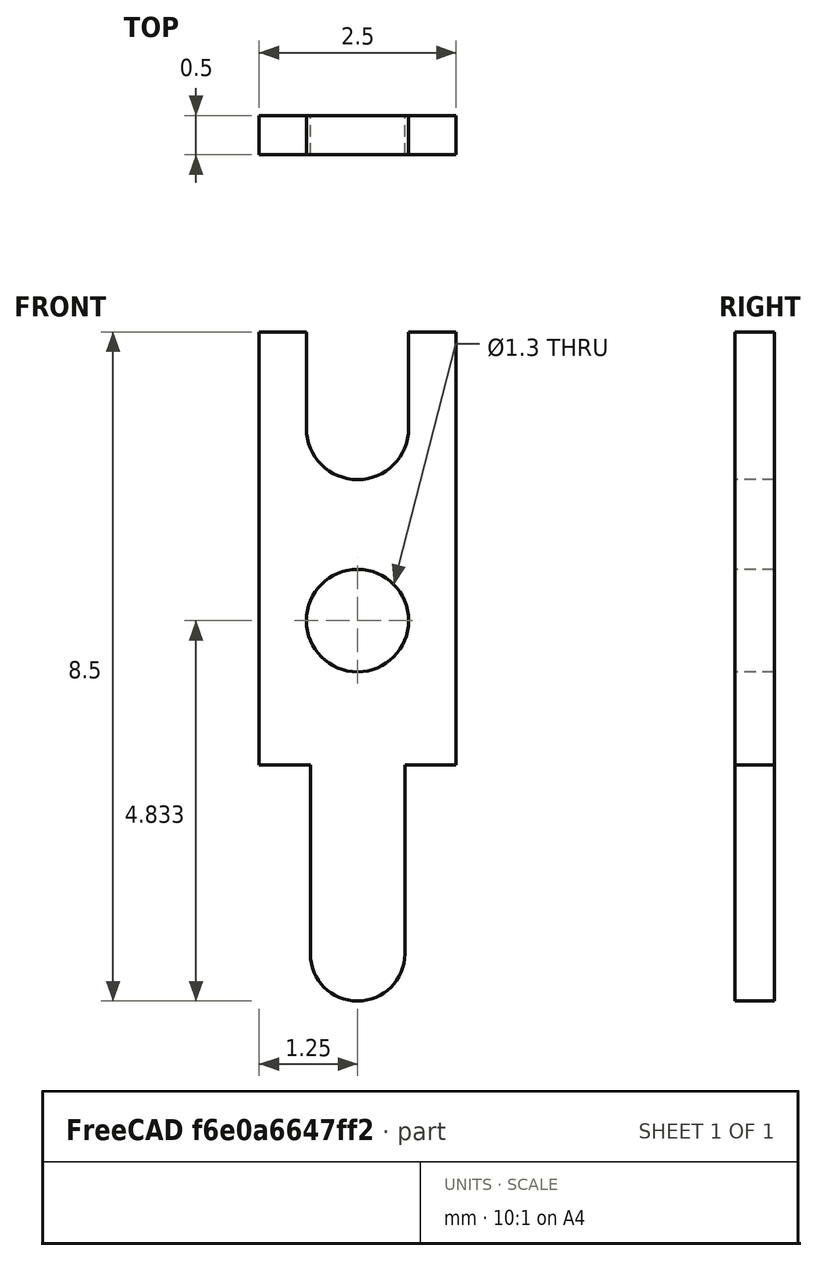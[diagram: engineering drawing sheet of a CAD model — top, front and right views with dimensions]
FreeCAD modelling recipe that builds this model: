
FCSTD DOCUMENT  (FreeCAD 0.17R12018 (Git))
Label: Pin_d1.1mm_L8.5mm_W2.5mm_FlatFork
License: All rights reserved
LicenseURL: http://en.wikipedia.org/wiki/All_rights_reserved
objects: Spreadsheet::Sheet×1, Sketcher::SketchObject×1, PartDesign::Pad×1, PartDesign::Body×1, App::Part×1
note: 4 computed .brp shape members not serialized (recipe doc carries the construction recipe); baked Part::Feature solids carry a one-line shape summary decoded from their .brp

FEATURE [Spreadsheet::Sheet] Spreadsheet  label="dimensions"
  cells = A1="L"; B1(L)=8.5; A2="Wtop"; B2(Wtop)=2.5; A3="Wbottom"; B3(Wbottom)=1.2; A4="Lbottom"; B4(Lbottom)=3; A5="Wfork"; B5(Wfork)=1.3; A6="FractionFork"; B6(FractionFork)=0.25; A7="thick"; B7(thick)=0.5
FEATURE [Sketcher::SketchObject] Sketch
  MapMode = 5
  Placement = pos=(0,0,0) rot=(0,0.707107,0.707107;3.14159rad)
  Support = -> [XZ_Plane001]
  expr: Constraints[44] = (dimensions.L - dimensions.Lbottom) * 0.66669999999999996
  expr: Constraints[43] = dimensions.Wfork / 2
  expr: Constraints[40] = dimensions.Wtop
  expr: Constraints[38] = dimensions.Wbottom
  expr: Constraints[39] = (dimensions.Wtop - dimensions.Wbottom) / 2
  expr: Constraints[37] = dimensions.Lbottom - dimensions.Wbottom / 2
  expr: Constraints[32] = dimensions.L - dimensions.Lbottom
  expr: Constraints[19] = dimensions.Wfork
  sketch-geometry (15):
    g0: LineSegment StartX=-1.25 StartY=5.5 StartZ=0 EndX=-1.25 EndY=0 EndZ=0
    g1: LineSegment StartX=-1.25 StartY=0 StartZ=0 EndX=-0.6 EndY=0 EndZ=0
    g2: LineSegment StartX=-0.6 StartY=0 StartZ=0 EndX=-0.6 EndY=-2.4 EndZ=0
    g3: LineSegment StartX=0.6 StartY=0 StartZ=0 EndX=0.6 EndY=-2.4 EndZ=0
    g4: LineSegment StartX=0.6 StartY=0 StartZ=0 EndX=1.25 EndY=0 EndZ=0
    g5: LineSegment StartX=1.25 StartY=0 StartZ=0 EndX=1.25 EndY=5.5 EndZ=0
    g6: LineSegment StartX=1.25 StartY=5.5 StartZ=0 EndX=0.65 EndY=5.5 EndZ=0
    g7: LineSegment StartX=0.65 StartY=5.5 StartZ=0 EndX=0.65 EndY=4.275 EndZ=0
    g8: LineSegment StartX=-0.65 StartY=4.275 StartZ=0 EndX=-0.65 EndY=5.5 EndZ=0
    g9: LineSegment StartX=-0.65 StartY=5.5 StartZ=0 EndX=-1.25 EndY=5.5 EndZ=0
    g10: ArcOfCircle CenterX=0 CenterY=-2.4 CenterZ=0 NormalX=0 NormalY=0 NormalZ=1 Radius=0.6 StartAngle=3.14159 EndAngle=6.28319
    g11: ArcOfCircle CenterX=0 CenterY=4.275 CenterZ=0 NormalX=0 NormalY=0 NormalZ=1 Radius=0.65 StartAngle=3.14159 EndAngle=6.28319
    g12: LineSegment [constr] StartX=-0.6 StartY=-2.4 StartZ=0 EndX=0.6 EndY=-2.4 EndZ=0
    g13: LineSegment [constr] StartX=-0.65 StartY=4.275 StartZ=0 EndX=0.65 EndY=4.275 EndZ=0
    g14: Circle CenterX=0 CenterY=1.83315 CenterZ=0 NormalX=0 NormalY=0 NormalZ=1 Radius=0.65
  constraints (45):
    c: PointOnObject(g3,g-1)
    c: Horizontal(g6)
    c: Vertical(g7)
    c: Vertical(g8)
    c: Coincident(g9,g0)
    c: Horizontal(g9)
    c: Equal(g9,g6)
    c: PointOnObject(g10,g-2)
    c: Coincident(g8,g9)
    c: Coincident(g6,g7)
    c: Coincident(g5,g6)
    c: Coincident(g11,g8)
    c: Coincident(g11,g7)
    c: Coincident(g12,g3)
    c: Coincident(g13,g8)
    c: Coincident(g13,g7)
    c: Horizontal(g13)
    c: PointOnObject(g11,g13)
    c: DistanceY(g8,g6) = 0
    c: DistanceX(g8,g6) = 1.3
    c: DistanceY(g8,g8) = 1.225
    c: Coincident(g12,g2)
    c: Coincident(g2,g10)
    c: Coincident(g3,g10)
    c: PointOnObject(g10,g12)
    c: Horizontal(g12)
    c: Vertical(g3)
    c: Vertical(g2)
    c: Horizontal(g1)
    c: Horizontal(g4)
    c: Vertical(g5)
    c: Vertical(g0)
    c: DistanceY(g5,g5) = 5.5
    c: Coincident(g5,g4)
    c: Coincident(g0,g1)
    c: Coincident(g4,g3)
    c: Coincident(g1,g2)
    c: DistanceY(g3,g3) = 2.4
    c: DistanceX(g2,g3) = 1.2
    c: DistanceX(g1,g1) = 0.65
    c: DistanceX(g0,g5) = 2.5
    c: PointOnObject(g1,g-1)
    c: PointOnObject(g14,g-2)
    c: Radius(g14) = 0.65
    c: DistanceY(g14,g8) = 3.66685
FEATURE [PartDesign::Pad] Pad
  Length = 0.5
  Length2 = 100
  Midplane = true
  Placement = pos=(0,0,0) rot=(1,0,0;1.5708rad)
  Profile = -> Sketch
  Type = 0
  expr: Length = dimensions.thick
FEATURE [PartDesign::Body] PadBody  label="Pin_d1.1mm_L8.5mm_W2.5mm_FlatFork"
  Group = -> [Sketch,Pad]
  Origin = -> Origin001
  Tip = -> Pad
FEATURE [App::Part] Part
  Group = -> [PadBody]
  License = CC BY 3.0
  LicenseURL = http://creativecommons.org/licenses/by/3.0/
  Origin = -> Origin
